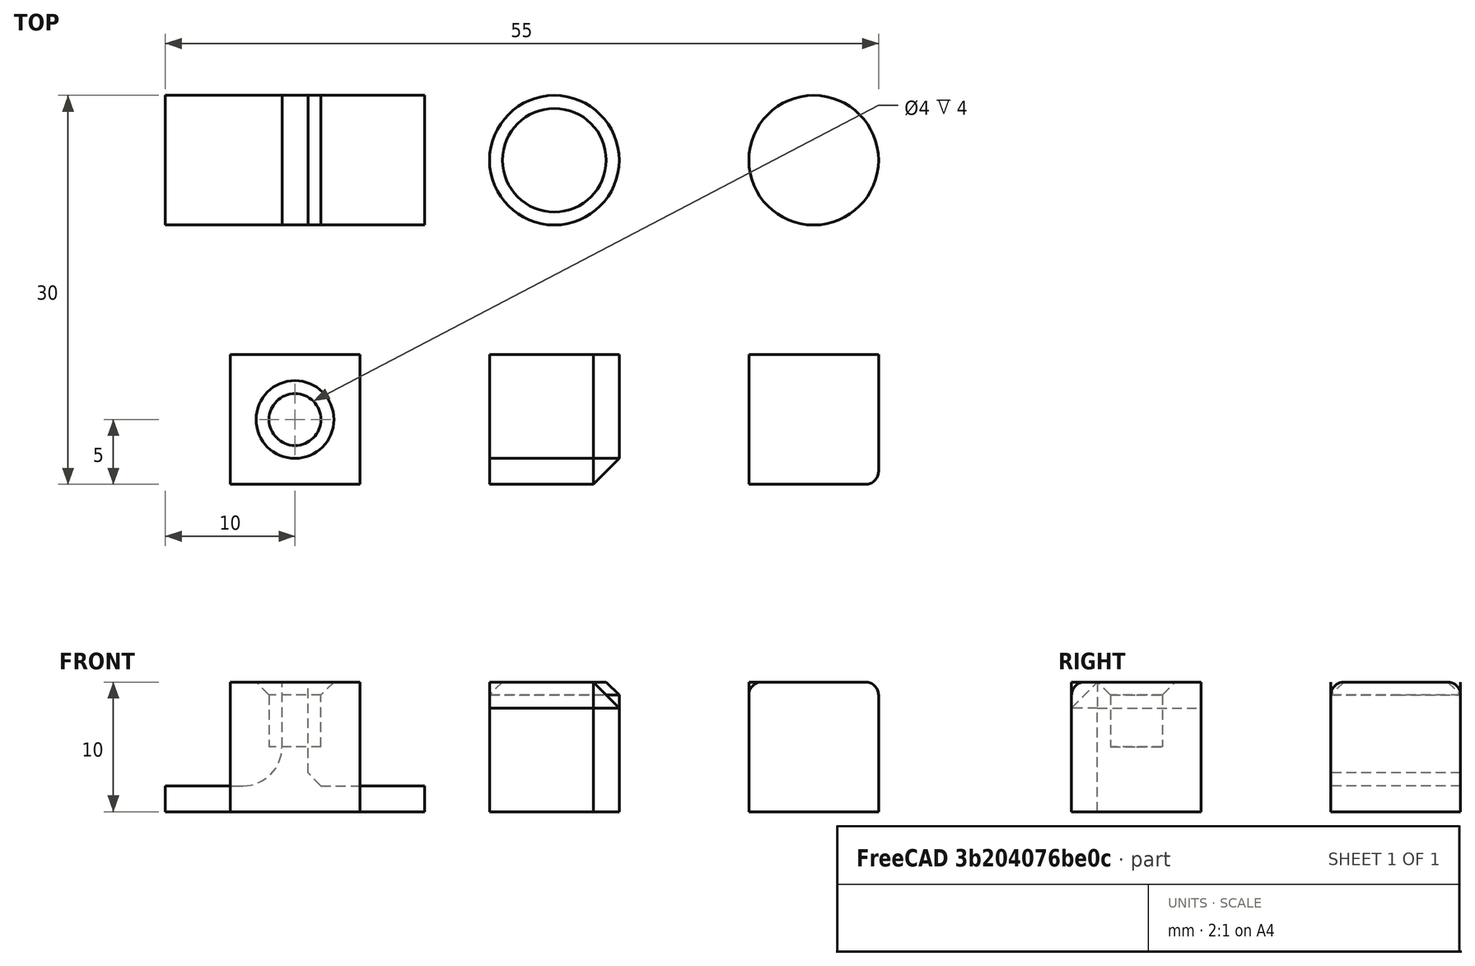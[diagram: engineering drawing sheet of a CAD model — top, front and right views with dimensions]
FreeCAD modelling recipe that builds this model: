
FCSTD DOCUMENT  (FreeCAD 1.0R39319 (Git))
Label: ojt1_t12p01_roundings_chamfers_reinforcements
License: All rights reserved
LicenseURL: https://en.wikipedia.org/wiki/All_rights_reserved
objects: Part::Box×5, Part::Chamfer×4, Part::Cylinder×3, Part::Fillet×3, Part::Cut×1, Part::MultiFuse×1
note: 17 computed .brp shape members not serialized (recipe doc carries the construction recipe); baked Part::Feature solids carry a one-line shape summary decoded from their .brp

FEATURE [Part::Box] Box  label="Cub"
  AttacherType = Attacher::AttachEngine3D
  Height = 10
  Length = 10
  Width = 10
FEATURE [Part::Box] Box001  label="cub 2"
  AttacherType = Attacher::AttachEngine3D
  Height = 10
  Length = 10
  Placement = pos=(20,0,0) rot=(0,0,1;0rad)
  Width = 10
FEATURE [Part::Box] Box002  label="cub 3"
  AttacherType = Attacher::AttachEngine3D
  Height = 10
  Length = 10
  Placement = pos=(40,0,0) rot=(0,0,1;0rad)
  Width = 10
FEATURE [Part::Cylinder] Cylinder  label="Cilindre"
  Angle = 360
  AttacherType = Attacher::AttachEngine3D
  FirstAngle = 0
  Height = 5
  Placement = pos=(5,5,5) rot=(0,0,1;0rad)
  Radius = 2
  SecondAngle = 0
FEATURE [Part::Cut] Cut  label="cub 1"
  Base = -> Box
  Refine = true
  Tool = -> Cylinder
FEATURE [Part::Fillet] Fillet
  Base = -> Box002
  EdgeLinks = -> Box002 [Edge5,Edge6,Edge10]
  Edges = 3 edges r=1: [Edge5,Edge6,Edge10]
FEATURE [Part::Chamfer] Chamfer
  Base = -> Box001
  EdgeLinks = -> Box001 [Edge5,Edge6,Edge10]
  Edges = 3 edges r=2: [Edge5,Edge6,Edge10]
FEATURE [Part::Chamfer] Chamfer001
  Base = -> Cut
  EdgeLinks = -> Cut [Edge10]
  Edges = 1 edges r=1: [Edge10]
FEATURE [Part::Cylinder] Cylinder001  label="Cilindre001"
  Angle = 360
  AttacherType = Attacher::AttachEngine3D
  FirstAngle = 0
  Height = 10
  Placement = pos=(45,25,0) rot=(0,0,1;0rad)
  Radius = 5
  SecondAngle = 0
FEATURE [Part::Cylinder] Cylinder002  label="Cilindre002"
  Angle = 360
  AttacherType = Attacher::AttachEngine3D
  FirstAngle = 0
  Height = 10
  Placement = pos=(25,25,0) rot=(0,0,1;0rad)
  Radius = 5
  SecondAngle = 0
FEATURE [Part::Fillet] Fillet001
  Base = -> Cylinder001
  EdgeLinks = -> Cylinder001 [Edge3]
  Edges = 1 edges r=1: [Edge3]
FEATURE [Part::Chamfer] Chamfer002
  Base = -> Cylinder002
  EdgeLinks = -> Cylinder002 [Edge3]
  Edges = 1 edges r=1: [Edge3]
FEATURE [Part::Box] Box003  label="Cub001"
  AttacherType = Attacher::AttachEngine3D
  Height = 2
  Length = 20
  Placement = pos=(-5,20,0) rot=(0,0,1;0rad)
  Width = 10
FEATURE [Part::Box] Box004  label="Cub002"
  AttacherType = Attacher::AttachEngine3D
  Height = 10
  Length = 2
  Placement = pos=(4,20,0) rot=(0,0,1;0rad)
  Width = 10
FEATURE [Part::MultiFuse] Fusion  label="T"
  Refine = true
  Shapes = -> [Box004,Box003]
FEATURE [Part::Chamfer] Chamfer003
  Base = -> Fusion
  EdgeLinks = -> Fusion [Edge7]
  Edges = 1 edges r=1: [Edge7]
FEATURE [Part::Fillet] Fillet002
  Base = -> Chamfer003
  EdgeLinks = -> Chamfer003 [Edge25]
  Edges = 1 edges r=3: [Edge25]
